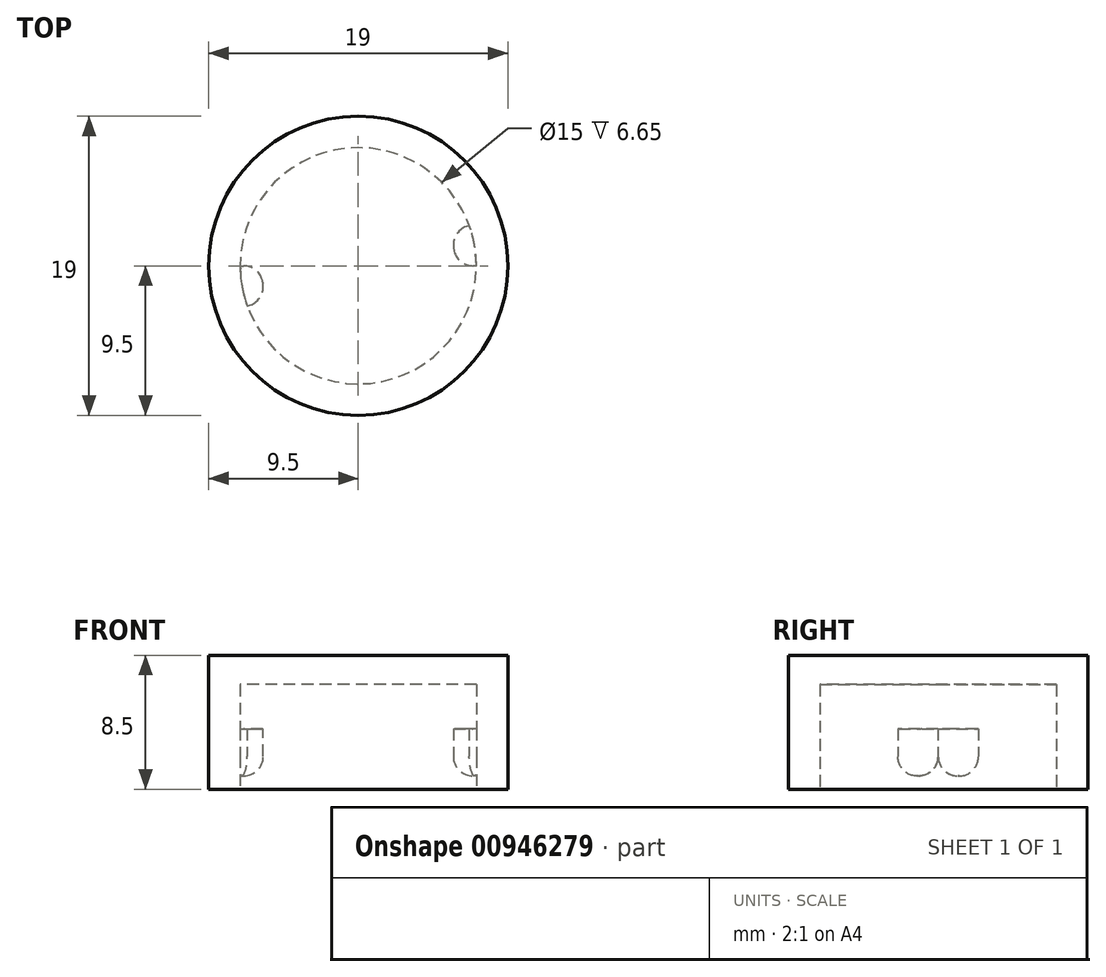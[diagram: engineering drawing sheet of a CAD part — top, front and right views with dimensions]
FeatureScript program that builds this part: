
annotation { "Feature Type Name" : "Feature", "Feature Type Description" : "" }
export const myFeature = defineFeature(function(context is Context, id is Id, definition is map)
    precondition{}
    {
        {
            assignVariable(context, id + "F0", {"name" : "tolerance", "anyValue" : .15});
        }
        {
            assignVariable(context, id + "F1", {"name" : "shell", "anyValue" : 2});
        }
        {
            assignVariable(context, id + "F2", {"name" : "nub_depth", "anyValue" : 1.25});
        }
        {
            assignVariable(context, id + "F3", {"name" : "nub_height", "anyValue" : 3});
        }
        {
            assignVariable(context, id + "F4", {"name" : "lock_base_height", "anyValue" : .7});
        }
        {
            assignVariable(context, id + "F5", {"name" : "lock_top_shelf", "anyValue" : 2.5});
        }
        {
            assignVariable(context, id + "F6", {"name" : "conn_height", "anyValue" : getVariable(context, 'lock_base_height') + getVariable(context, 'nub_height') + getVariable(context, 'lock_top_shelf') + getVariable(context, 'tolerance') * 2});
        }
        {
            var Q0;
            Q0=qCreatedBy(makeId("Top.planeOp"),FACE);
            var sketch = newSketch(context, id + "F7", { "sketchPlane" : qUnion([Q0])});
            skCircle(sketch, "E0", {"center": v(0, 0) * mm, "radius": 7.5 * mm});
            skCircle(sketch, "E1.0", {"center": v(0, 0) * mm, "radius": 9.5 * mm});
            skLineSegment(sketch, "E2", {"start": v(7.5, 0) * mm, "end": v(6.25, 0) * mm});
            skLineSegment(sketch, "E3", {"start": v(-7.5, 0) * mm, "end": v(-6.25, 0) * mm});
            skLineSegment(sketch, "E4", {"start": v(0, 0) * mm, "end": v(7.5, 0) * mm, "construction": true});
            skLineSegment(sketch, "E5", {"start": v(0, 0) * mm, "end": v(7.05, 2.57) * mm, "construction": true});
            skLineSegment(sketch, "E6", {"start": v(0, 0) * mm, "end": v(-7.5, 0) * mm, "construction": true});
            skLineSegment(sketch, "E7", {"start": v(0, 0) * mm, "end": v(-7.05, -2.57) * mm, "construction": true});
            skLineSegment(sketch, "E8", {"start": v(-7.05, -2.57) * mm, "end": v(-5.87, -2.14) * mm});
            skLineSegment(sketch, "E9", {"start": v(7.05, 2.57) * mm, "end": v(5.87, 2.14) * mm});
            skLineSegment(sketch, "E10", {"start": v(-6.25, 0) * mm, "end": v(-5.87, -2.14) * mm});
            skLineSegment(sketch, "E11", {"start": v(5.87, 2.14) * mm, "end": v(6.25, 0) * mm});
            skSolve(sketch);
        }
        {
            var Q0;
            Q0=makeQuery(id+"F7.imprint","IMPRINT",FACE,{"disambiguationData":[TD([[makeQuery(id+"F7.imprint","IMPRINT",EDGE,{"derivedFrom":sQuery(id+"F7.wireOp",EDGE,"E1.0")}),1.0]])]});
            extrude(context, id + "F8", {"entities" : qUnion([Q0]), "depth" : (getVariable(context, 'conn_height') + getVariable(context, 'tolerance')) * mm, "offsetDistance" : 25 * mm});
        }
        {
            var Q0;
            Q0=makeQuery(id+"F7.imprint","IMPRINT",FACE,{"disambiguationData":[TD([[makeQuery(id+"F7.imprint","IMPRINT",EDGE,{"derivedFrom":sQuery(id+"F7.wireOp",EDGE,"E1.0")}),1.0]])]});
            var Q1;
            {var subQ0=sQuery(id+"F7.wireOp",EDGE,"E3");Q1=makeQuery(id+"F7.imprint","IMPRINT",FACE,{"disambiguationData":[TD([[makeQuery(id+"F7.imprint","IMPRINT",EDGE,{"derivedFrom":subQ0}),-1.0]])]});}
            var Q2;
            {var subQ0=sQuery(id+"F7.wireOp",EDGE,"E2");Q2=makeQuery(id+"F7.imprint","IMPRINT",FACE,{"disambiguationData":[TD([[makeQuery(id+"F7.imprint","IMPRINT",EDGE,{"derivedFrom":subQ0}),1.0]])]});}
            var Q3;
            {var subQ0=sQuery(id+"F7.wireOp",EDGE,"E2");Q3=makeQuery(id+"F7.imprint","IMPRINT",FACE,{"disambiguationData":[TD([[makeQuery(id+"F7.imprint","IMPRINT",EDGE,{"derivedFrom":subQ0}),-1.0]])]});}
            extrude(context, id + "F9", {"entities" : qUnion([Q0, Q1, Q2, Q3]), "operationType" : NewBodyOperationType.ADD, "depth" : (getVariable(context, 'conn_height') + getVariable(context, 'shell')) * mm, "offsetDistance" : 25 * mm, "hasSecondDirection" : true, "secondDirectionOppositeDirection" : false, "secondDirectionDepth" : (getVariable(context, 'conn_height') + getVariable(context, 'tolerance')) * mm});
        }
        {
            var Q0;
            {var subQ0=sQuery(id+"F7.wireOp",EDGE,"E3");Q0=makeQuery(id+"F7.imprint","IMPRINT",FACE,{"disambiguationData":[TD([[makeQuery(id+"F7.imprint","IMPRINT",EDGE,{"derivedFrom":subQ0}),-1.0]])]});}
            var Q1;
            {var subQ0=sQuery(id+"F7.wireOp",EDGE,"E2");Q1=makeQuery(id+"F7.imprint","IMPRINT",FACE,{"disambiguationData":[TD([[makeQuery(id+"F7.imprint","IMPRINT",EDGE,{"derivedFrom":subQ0}),-1.0]])]});}
            extrude(context, id + "F10", {"entities" : qUnion([Q0, Q1]), "operationType" : NewBodyOperationType.ADD, "depth" : (getVariable(context, 'lock_base_height') + getVariable(context, 'nub_height') + getVariable(context, 'tolerance')) * mm, "offsetDistance" : 25 * mm, "hasSecondDirection" : true, "secondDirectionOppositeDirection" : false, "secondDirectionDepth" : (getVariable(context, 'lock_base_height') + getVariable(context, 'tolerance')) * mm});
        }
        {
            var Q0;
            Q0=makeQuery(id+"F10.opExtrude","SWEPT_EDGE",EDGE,{"disambiguationData":[OSD([sQuery(id+"F7.wireOp",EDGE,"E8"),sQuery(id+"F7.wireOp",EDGE,"E10")])]});
            var Q1;
            Q1=makeQuery(id+"F10.opExtrude","SWEPT_EDGE",EDGE,{"disambiguationData":[OSD([sQuery(id+"F7.wireOp",EDGE,"E3"),sQuery(id+"F7.wireOp",EDGE,"E10")])]});
            var Q2;
            Q2=makeQuery(id+"F10.opExtrude","SWEPT_EDGE",EDGE,{"disambiguationData":[OSD([sQuery(id+"F7.wireOp",EDGE,"E2"),sQuery(id+"F7.wireOp",EDGE,"E11")])]});
            var Q3;
            Q3=makeQuery(id+"F10.opExtrude","SWEPT_EDGE",EDGE,{"disambiguationData":[OSD([sQuery(id+"F7.wireOp",EDGE,"E9"),sQuery(id+"F7.wireOp",EDGE,"E11")])]});
            fillet(context, id + "F11", {"entities" : qUnion([Q0, Q1, Q2, Q3]), "radius" : (getVariable(context, 'nub_depth')) * mm, "tangentPropagation" : true, "allowEdgeOverflow" : false});
        }
        {
            var Q0;
            {var subQ0=sQuery(id+"F7.wireOp",EDGE,"E10");var subQ1=sQuery(id+"F7.wireOp",EDGE,"E8");Q0=makeQuery(id+"F11.opFillet","BLEND_EDGE",EDGE,{"blendedFrom":[makeQuery(id+"F10.opExtrude","SWEPT_EDGE",EDGE,{"disambiguationData":[OSD([subQ1,subQ0])]}),makeQuery(id+"F10.opExtrude","CAP_FACE",FACE,{"disambiguationData":[OSD([sQuery(id+"F7.wireOp",EDGE,"E0"),sQuery(id+"F7.wireOp",EDGE,"E3"),subQ1,subQ0])],"isStart":true})],"blendedInto":[makeQuery(id+"F10.opExtrude","CAP_FACE",FACE,{"disambiguationData":[OSD([sQuery(id+"F7.wireOp",EDGE,"E0"),sQuery(id+"F7.wireOp",EDGE,"E3"),subQ1,subQ0])],"isStart":true})]});}
            var Q1;
            {var subQ0=sQuery(id+"F7.wireOp",EDGE,"E11");var subQ1=sQuery(id+"F7.wireOp",EDGE,"E2");Q1=makeQuery(id+"F11.opFillet","BLEND_EDGE",EDGE,{"blendedFrom":[makeQuery(id+"F10.opExtrude","SWEPT_EDGE",EDGE,{"disambiguationData":[OSD([subQ1,subQ0])]}),makeQuery(id+"F10.opExtrude","CAP_FACE",FACE,{"disambiguationData":[OSD([sQuery(id+"F7.wireOp",EDGE,"E0"),subQ1,sQuery(id+"F7.wireOp",EDGE,"E9"),subQ0])],"isStart":true})],"blendedInto":[makeQuery(id+"F10.opExtrude","CAP_FACE",FACE,{"disambiguationData":[OSD([sQuery(id+"F7.wireOp",EDGE,"E0"),subQ1,sQuery(id+"F7.wireOp",EDGE,"E9"),subQ0])],"isStart":true})]});}
            fillet(context, id + "F12", {"entities" : qUnion([Q0, Q1]), "radius" : (getVariable(context, 'nub_depth')) * mm, "tangentPropagation" : true, "allowEdgeOverflow" : false});
        }
    });
